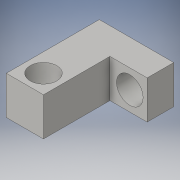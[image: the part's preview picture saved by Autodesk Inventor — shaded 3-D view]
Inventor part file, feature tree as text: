
AUTODESK INVENTOR PART (.ipt)
format: ipt  version: 2016 (Build 200138000, 138)  size: 109,568 bytes
history: native  units: in
note: dims shown in document units (in); Inventor stores cm internally (conversion verified against a paired STEP export)
features: extrude x3, sketch x3
ambient origin geometry x8: Origin, YZ Plane, XZ Plane, XY Plane, X Axis, Y Axis, Z Axis, Center Point
bodies: Solid1 (feature_tree)
feature tree (6):
  extrude  "Extrusion1"  Depth=1.75in
  extrude  "Extrusion2"  Depth=0.5in
  extrude  "Extrusion3"  Depth=0.5in
  sketch  "Sketch1"  dims[d0=0.7in d1=1.75in]
  sketch  "Sketch2"  dims[d2=0.7in d3=0.5in]
  sketch  "Sketch3"  dims[d4=0.72in d5=0.0in d6=0.5in d7=0.5in d8=0.0in d9=0.5in d10=0.35in d11=0.72in d12=0.0in]
